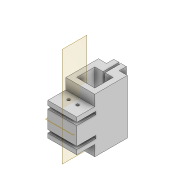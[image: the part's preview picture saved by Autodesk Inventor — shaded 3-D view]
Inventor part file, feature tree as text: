
AUTODESK INVENTOR PART (.ipt)
format: ipt  version: 2022 (Build 260153000, 153)  size: 205,824 bytes
history: native  units: mm
features: extrude x6, sketch x6, projected_geometry x4, plane x2
ambient origin geometry x8: Origin, YZ Plane, XZ Plane, XY Plane, X Axis, Y Axis, Z Axis, Center Point
bodies: Solid1 (feature_tree)
feature tree (18):
  extrude  "Extrusion1"  Depth=60.0mm
  extrude  "Extrusion2"  Depth=30.0mm
  extrude  "Extrusion3"  Depth=60.0mm
  plane  "Work Plane1"
  plane  "Work Plane3"
  extrude  "Extrusion12"  Depth=5.0mm
  extrude  "Extrusion13"  Depth=3.2mm
  extrude  "Extrusion14"  Depth=20.0mm TaperAngle=0.0deg
  sketch  "Sketch1"  dims[d0=32.0mm d1=60.0mm]
  sketch  "Sketch3"  dims[d2=6.0mm d3=0.0mm d6=30.0mm]
  projected_geometry  "Projected Loop2"
  sketch  "Sketch4"  dims[d7=60.0mm d8=9.9mm]
  projected_geometry  "Projected Loop3"
  sketch  "Sketch14"  dims[d9=9.9mm d10=5.0mm]
  sketch  "Sketch15"  dims[d11=3.2mm d12=3.2mm]
  sketch  "Sketch16"  dims[d13=5.0mm d14=20.0mm d15=0.0mm d16=3.1mm d17=3.1mm d18=4.95mm d19=4.95mm d20=8.0mm d21=8.0mm d22=100.0mm d23=0.0mm d74=20.2mm d75=20.2mm d76=30.0mm d77=5.9mm d78=32.0mm d79=1.0mm d80=1.0mm d81=6.0mm d82=6.0mm d83=8.0mm d85=8.0mm d86=60.0mm d87=0.0mm d88=3.2mm d89=3.2mm d90=3.2mm d91=10.0mm d92=10.0mm d93=30.0mm d94=4.0mm d95=60.0mm d96=0.0mm d97=1.0mm d98=0.0mm]
  projected_geometry  "Projected Loop15"
  projected_geometry  "Projected Loop16"
